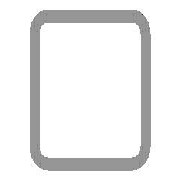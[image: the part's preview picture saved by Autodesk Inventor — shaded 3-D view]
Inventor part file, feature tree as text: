
AUTODESK INVENTOR PART (.ipt)
format: ipt  version: 2018 (Build 220112000, 112)  size: 144,896 bytes
history: native  units: mm (DEFAULTED — no unit token found)
features: sketch x4, other x3, extrude x1, hole x1, plane x1
ambient origin geometry x8: Origin, YZ Plane, XZ Plane, XY Plane, X Axis, Y Axis, Z Axis, Center Point
bodies: Solid1 (feature_tree)
feature tree (10):
  other  "Driven Length"
  other  "Piano iniziale"
  other  "Piano finale"
  extrude  "Corpo"  TaperAngle=0.0deg  [1 undecoded]
  hole  "Foro1"  [1 undecoded]
  sketch  "Schizzo"
  sketch  "Sketch3"  dims[d3=235.0mm d4=0.0mm]
  plane  "Work Plane3"
  sketch  "Sketch4"  dims[d7=4.0mm d9=20.0mm d11=20.0mm d12=2.0mm d13=-0.0mm d14=235.0mm d15=10.0mm d16=10.0mm d17=90.0deg d18=235.0mm d19=10.0mm d20=6.0mm d21=4.0mm d22=2.0mm d23=90.0deg d24=8.0mm d25=20.594885mm d26=11.5mm d27=27.0mm d28=9.912445mm]
  sketch  "Schizzo5"
note: 2 required parameter values undecoded (feature->parameter linkage not recoverable at this tier; creation-order binding heuristic only, values carry confidence <= 0.55)
